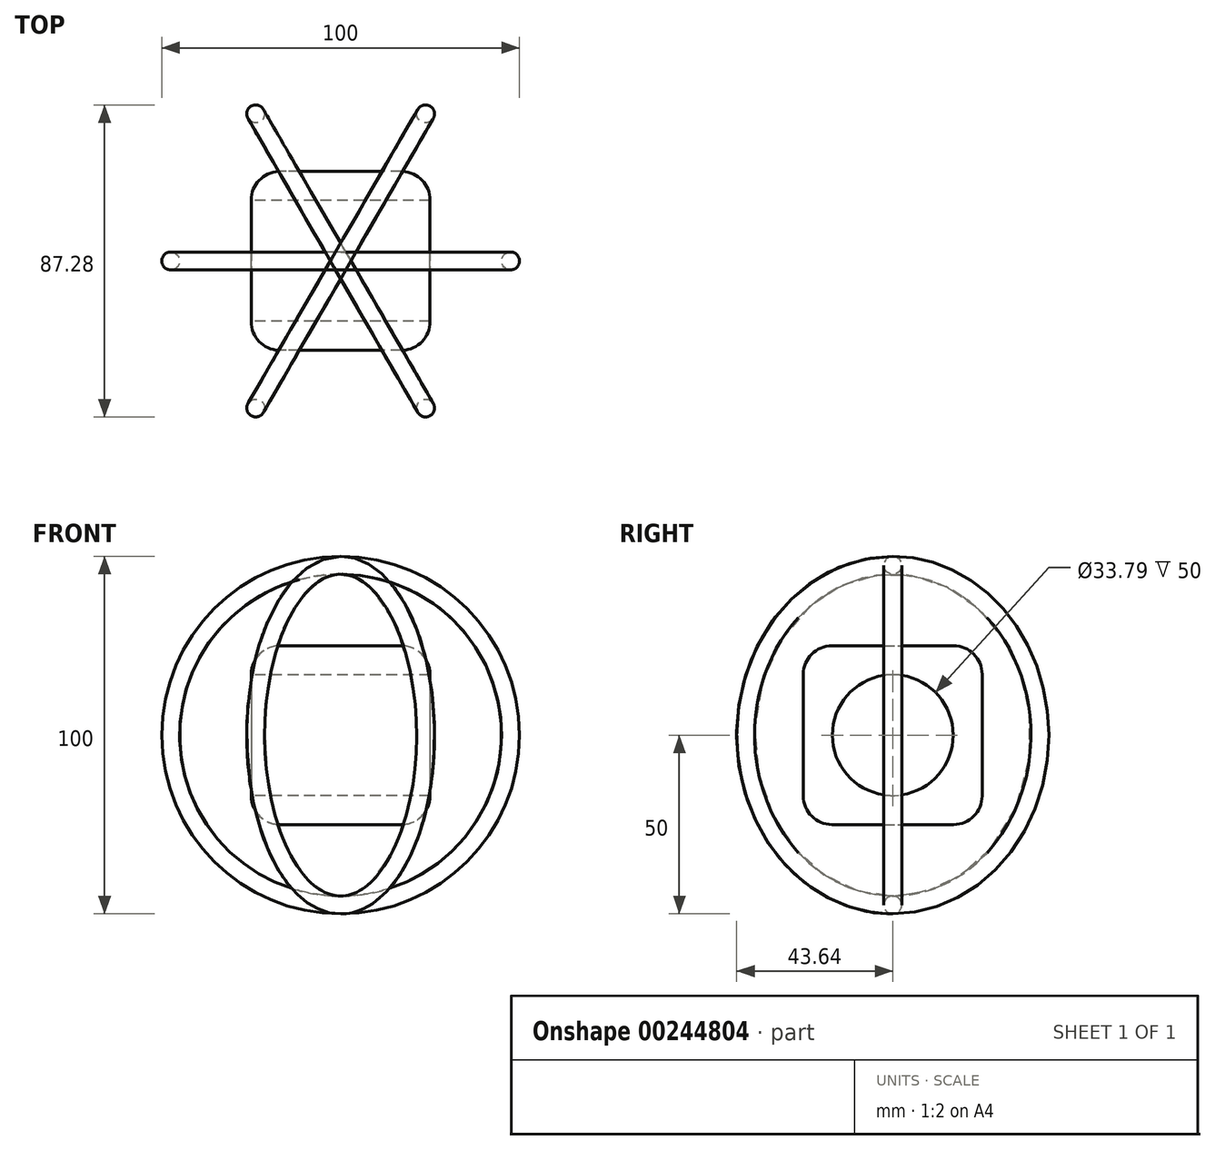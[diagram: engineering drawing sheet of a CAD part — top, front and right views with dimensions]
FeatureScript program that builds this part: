
annotation { "Feature Type Name" : "Feature", "Feature Type Description" : "" }
export const myFeature = defineFeature(function(context is Context, id is Id, definition is map)
    precondition{}
    {
        {
            var Q0;
            Q0=qCreatedBy(makeId("Top.planeOp"),FACE);
            var sketch = newSketch(context, id + "F0", { "sketchPlane" : qUnion([Q0])});
            skLineSegment(sketch, "E0.bottom", {"start": v(25, -25) * mm, "end": v(-25, -25) * mm});
            skLineSegment(sketch, "E0.top", {"start": v(25, 25) * mm, "end": v(-25, 25) * mm});
            skLineSegment(sketch, "E0.left", {"start": v(25, -25) * mm, "end": v(25, 25) * mm});
            skLineSegment(sketch, "E0.right", {"start": v(-25, -25) * mm, "end": v(-25, 25) * mm});
            skPoint(sketch, "E0.middle", {"position": v(0, 0) * mm});
            skSolve(sketch);
        }
        {
            var Q0;
            Q0=makeQuery(id+"F0.imprint","IMPRINT",FACE,{"disambiguationData":[TD([[makeQuery(id+"F0.imprint","IMPRINT",EDGE,{"derivedFrom":sQuery(id+"F0.wireOp",EDGE,"E0.bottom")}),-1.0]])]});
            extrude(context, id + "F1", {"entities" : qUnion([Q0]), "depth" : 25 * mm, "hasSecondDirection" : true, "secondDirectionOppositeDirection" : true, "secondDirectionDepth" : 25 * mm});
        }
        {
            var Q0;
            Q0=qCreatedBy(makeId("Front.planeOp"),FACE);
            var sketch = newSketch(context, id + "F2", { "sketchPlane" : qUnion([Q0])});
            skCircle(sketch, "E1", {"center": v(0, 0) * mm, "radius": 50 * mm});
            skCircle(sketch, "E2.0", {"center": v(0, 0) * mm, "radius": 45 * mm});
            skSolve(sketch);
        }
        {
            var Q0;
            Q0=makeQuery(id+"F2.imprint","IMPRINT",FACE,{"disambiguationData":[TD([[makeQuery(id+"F2.imprint","IMPRINT",EDGE,{"derivedFrom":sQuery(id+"F2.wireOp",EDGE,"E1")}),1.0]])]});
            extrude(context, id + "F3", {"entities" : qUnion([Q0]), "depth" : 2.5 * mm, "hasSecondDirection" : true, "secondDirectionOppositeDirection" : true, "secondDirectionDepth" : 2.5 * mm});
        }
        {
            var Q0;
            Q0=makeQuery(id+"F3.opExtrude","CAP_EDGE",EDGE,{"disambiguationData":[OSD([sQuery(id+"F2.wireOp",EDGE,"E1")])],"isStart":false});
            var Q1;
            Q1=makeQuery(id+"F3.opExtrude","CAP_EDGE",EDGE,{"disambiguationData":[OSD([sQuery(id+"F2.wireOp",EDGE,"E2.0")])],"isStart":false});
            var Q2;
            Q2=makeQuery(id+"F3.opExtrude","SWEPT_FACE",FACE,{"disambiguationData":[OSD([sQuery(id+"F2.wireOp",EDGE,"E1")])]});
            var Q3;
            Q3=makeQuery(id+"F3.opExtrude","CAP_EDGE",EDGE,{"disambiguationData":[OSD([sQuery(id+"F2.wireOp",EDGE,"E2.0")])],"isStart":true});
            fillet(context, id + "F4", {"entities" : qUnion([Q0, Q1, Q2, Q3]), "radius" : 2.5 * mm, "tangentPropagation" : true, "allowEdgeOverflow" : false});
        }
        {
            var Q0;
            Q0=qCreatedBy(makeId("Top.planeOp"),FACE);
            var sketch = newSketch(context, id + "F5", { "sketchPlane" : qUnion([Q0])});
            skCircle(sketch, "E3", {"center": v(0, 0) * mm, "radius": 50 * mm});
            skSolve(sketch);
        }
        {
            var Q0;
            Q0=makeQuery(id+"F3.opExtrude","SWEPT_BODY",BODY,{"disambiguationData":[OSD([sQuery(id+"F2.wireOp",EDGE,"E1"),sQuery(id+"F2.wireOp",EDGE,"E2.0")])]});
            var Q1;
            Q1=sQuery(id+"F5.wireOp",EDGE,"E3");
            circularPattern(context, id + "F6", {"operationType" : NewBodyOperationType.ADD, "entities" : qUnion([Q0]), "axis" : qUnion([Q1]), "angle" : 360 * degree, "instanceCount" : 6, "equalSpace" : true});
        }
        {
            var Q0;
            Q0=makeQuery(id+"F1.opExtrude","CAP_EDGE",EDGE,{"disambiguationData":[OSD([sQuery(id+"F0.wireOp",EDGE,"E0.bottom")])],"isStart":false});
            var Q1;
            Q1=makeQuery(id+"F1.opExtrude","CAP_EDGE",EDGE,{"disambiguationData":[OSD([sQuery(id+"F0.wireOp",EDGE,"E0.right")])],"isStart":false});
            var Q2;
            Q2=makeQuery(id+"F1.opExtrude","CAP_EDGE",EDGE,{"disambiguationData":[OSD([sQuery(id+"F0.wireOp",EDGE,"E0.top")])],"isStart":false});
            var Q3;
            Q3=makeQuery(id+"F1.opExtrude","CAP_EDGE",EDGE,{"disambiguationData":[OSD([sQuery(id+"F0.wireOp",EDGE,"E0.right")])],"isStart":true});
            var Q4;
            Q4=makeQuery(id+"F1.opExtrude","SWEPT_EDGE",EDGE,{"disambiguationData":[OSD([sQuery(id+"F0.wireOp",EDGE,"E0.bottom"),sQuery(id+"F0.wireOp",EDGE,"E0.right")])]});
            var Q5;
            Q5=makeQuery(id+"F1.opExtrude","CAP_EDGE",EDGE,{"disambiguationData":[OSD([sQuery(id+"F0.wireOp",EDGE,"E0.bottom")])],"isStart":true});
            var Q6;
            Q6=makeQuery(id+"F1.opExtrude","SWEPT_EDGE",EDGE,{"disambiguationData":[OSD([sQuery(id+"F0.wireOp",EDGE,"E0.bottom"),sQuery(id+"F0.wireOp",EDGE,"E0.left")])]});
            var Q7;
            Q7=makeQuery(id+"F1.opExtrude","CAP_EDGE",EDGE,{"disambiguationData":[OSD([sQuery(id+"F0.wireOp",EDGE,"E0.left")])],"isStart":false});
            var Q8;
            Q8=makeQuery(id+"F1.opExtrude","CAP_EDGE",EDGE,{"disambiguationData":[OSD([sQuery(id+"F0.wireOp",EDGE,"E0.left")])],"isStart":true});
            var Q9;
            Q9=makeQuery(id+"F1.opExtrude","SWEPT_EDGE",EDGE,{"disambiguationData":[OSD([sQuery(id+"F0.wireOp",EDGE,"E0.top"),sQuery(id+"F0.wireOp",EDGE,"E0.left")])]});
            var Q10;
            Q10=makeQuery(id+"F1.opExtrude","CAP_EDGE",EDGE,{"disambiguationData":[OSD([sQuery(id+"F0.wireOp",EDGE,"E0.top")])],"isStart":true});
            var Q11;
            Q11=makeQuery(id+"F1.opExtrude","SWEPT_EDGE",EDGE,{"disambiguationData":[OSD([sQuery(id+"F0.wireOp",EDGE,"E0.top"),sQuery(id+"F0.wireOp",EDGE,"E0.right")])]});
            fillet(context, id + "F7", {"entities" : qUnion([Q0, Q1, Q2, Q3, Q4, Q5, Q6, Q7, Q8, Q9, Q10, Q11]), "radius" : 8 * mm, "tangentPropagation" : true, "allowEdgeOverflow" : false});
        }
        {
            var Q0;
            Q0=makeQuery(id+"F1.opExtrude","SWEPT_FACE",FACE,{"disambiguationData":[OSD([sQuery(id+"F0.wireOp",EDGE,"E0.right")])]});
            var sketch = newSketch(context, id + "F8", { "sketchPlane" : qUnion([Q0])});
            skCircle(sketch, "E4", {"center": v(0, 0) * mm, "radius": 16.9 * mm});
            skSolve(sketch);
        }
        {
            var Q0;
            Q0=makeQuery(id+"F8.imprint","IMPRINT",FACE,{"disambiguationData":[TD([[makeQuery(id+"F8.imprint","IMPRINT",EDGE,{"derivedFrom":sQuery(id+"F8.wireOp",EDGE,"E4")}),1.0]])]});
            extrude(context, id + "F9", {"entities" : qUnion([Q0]), "operationType" : NewBodyOperationType.REMOVE, "oppositeDirection" : true, "depth" : 50 * mm});
        }
    });
